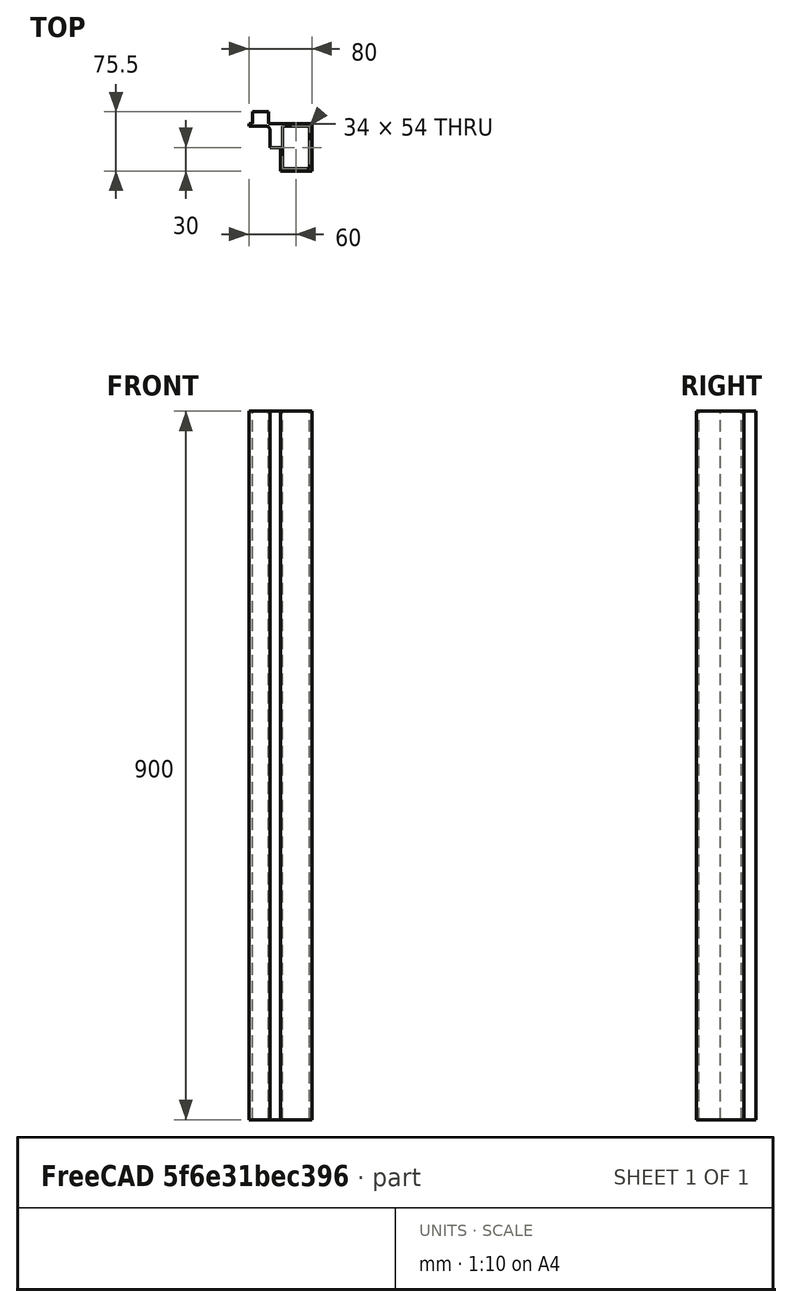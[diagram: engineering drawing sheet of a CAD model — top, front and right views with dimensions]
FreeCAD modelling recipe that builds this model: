
FCSTD DOCUMENT  (FreeCAD 0.21R33771 (Git))
Label: Tubolare60x40-base
License: All rights reserved
LicenseURL: http://en.wikipedia.org/wiki/All_rights_reserved
objects: Sketcher::SketchObject×1, PartDesign::Pad×1, PartDesign::CoordinateSystem×1, PartDesign::Body×1
note: 5 computed .brp shape members not serialized (recipe doc carries the construction recipe); baked Part::Feature solids carry a one-line shape summary decoded from their .brp

FEATURE [Sketcher::SketchObject] Sketch
  FullyConstrained = true
  MapMode = 5
  Support = -> [XY_Plane]
  sketch-geometry (17):
    g0: LineSegment StartX=0 StartY=0 StartZ=0 EndX=40 EndY=0 EndZ=0
    g1: LineSegment StartX=40 StartY=0 StartZ=0 EndX=40 EndY=60 EndZ=0
    g2: LineSegment StartX=40 StartY=60 StartZ=0 EndX=-15 EndY=60 EndZ=0
    g3: LineSegment StartX=0 StartY=30 StartZ=0 EndX=0 EndY=0 EndZ=0
    g4: LineSegment StartX=3 StartY=57 StartZ=0 EndX=37 EndY=57 EndZ=0
    g5: LineSegment StartX=37 StartY=57 StartZ=0 EndX=37 EndY=3 EndZ=0
    g6: LineSegment StartX=37 StartY=3 StartZ=0 EndX=3 EndY=3 EndZ=0
    g7: LineSegment StartX=3 StartY=3 StartZ=0 EndX=3 EndY=57 EndZ=0
    g8: LineSegment StartX=-40 StartY=60 StartZ=0 EndX=-40 EndY=57 EndZ=0
    g9: LineSegment StartX=-40 StartY=57 StartZ=0 EndX=-18 EndY=57 EndZ=0
    g10: LineSegment StartX=-13 StartY=52 StartZ=0 EndX=-13 EndY=30 EndZ=0
    g11: LineSegment StartX=-13 StartY=30 StartZ=0 EndX=0 EndY=30 EndZ=0
    g12: ArcOfCircle CenterX=-18 CenterY=52 CenterZ=0 NormalX=0 NormalY=0 NormalZ=1 AngleXU=0 Radius=5 StartAngle=-5.3e-15 EndAngle=1.5708
    g13: LineSegment StartX=-35 StartY=60 StartZ=0 EndX=-35 EndY=75.5 EndZ=0
    g14: LineSegment StartX=-35 StartY=75.5 StartZ=0 EndX=-15 EndY=75.5 EndZ=0
    g15: LineSegment StartX=-15 StartY=75.5 StartZ=0 EndX=-15 EndY=60 EndZ=0
    g16: LineSegment StartX=-35 StartY=60 StartZ=0 EndX=-40 EndY=60 EndZ=0
  constraints (48):
    c: Coincident(g0,g1)
    c: Coincident(g1,g2)
    c: Coincident(g3,g0)
    c: Horizontal(g0)
    c: Horizontal(g2)
    c: Vertical(g1)
    c: Vertical(g3)
    c: Coincident(g0,g-1)
    c: DistanceX(g0,g0) = 40
    c: DistanceY(g1,g1) = 60
    c: Coincident(g4,g5)
    c: Coincident(g5,g6)
    c: Coincident(g6,g7)
    c: Coincident(g7,g4)
    c: Horizontal(g4)
    c: Horizontal(g6)
    c: Vertical(g5)
    c: Vertical(g7)
    c: DistanceX(g6,g6) = 34
    c: DistanceY(g5,g5) = 54
    c: DistanceX(g0,g6) = 3
    c: DistanceY(g0,g6) = 3
    c: Vertical(g8)
    c: Coincident(g9,g8)
    c: Horizontal(g9)
    c: Vertical(g10)
    c: Coincident(g11,g10)
    c: Horizontal(g11)
    c: Coincident(g3,g11)
    c: Coincident(g16,g8)
    c: DistanceX(g16,g2) = 80
    c: DistanceY(g8,g8) = 3
    c: Tangent(g10,g12) = 1.5708
    c: Tangent(g9,g12) = 1.5708
    c: Radius(g12) = 5
    c: DistanceX(g9,g9) = 22
    c: DistanceY(g10,g10) = 22
    c: Vertical(g13)
    c: Horizontal(g14)
    c: Coincident(g15,g14)
    c: Vertical(g15)
    c: Coincident(g13,g14)
    c: Coincident(g2,g15)
    c: Coincident(g16,g13)
    c: Tangent(g2,g16)
    c: DistanceX(g14,g14) = 20
    c: DistanceX(g16,g16) = 5
    c: DistanceY(g15,g15) = 15.5
FEATURE [PartDesign::Pad] Pad
  Direction = (0,0,1)
  Length = 900
  Length2 = 100
  Profile = -> Sketch
  ReferenceAxis = -> Sketch [N_Axis]
  Type = 0
FEATURE [PartDesign::CoordinateSystem] LCS_1
  AttacherType = Attacher::AttachEngine3D
  AttachmentOffset = pos=(0,-2,0) rot=(0,0,1;0rad)
  MapMode = 7
  Placement = pos=(40,-4e-16,-2) rot=(1,0,0;1.5708rad)
  Support = -> [Pad]
FEATURE [PartDesign::Body] Body
  Group = -> [Sketch,Pad,LCS_1]
  Origin = -> Origin
  Tip = -> Pad
